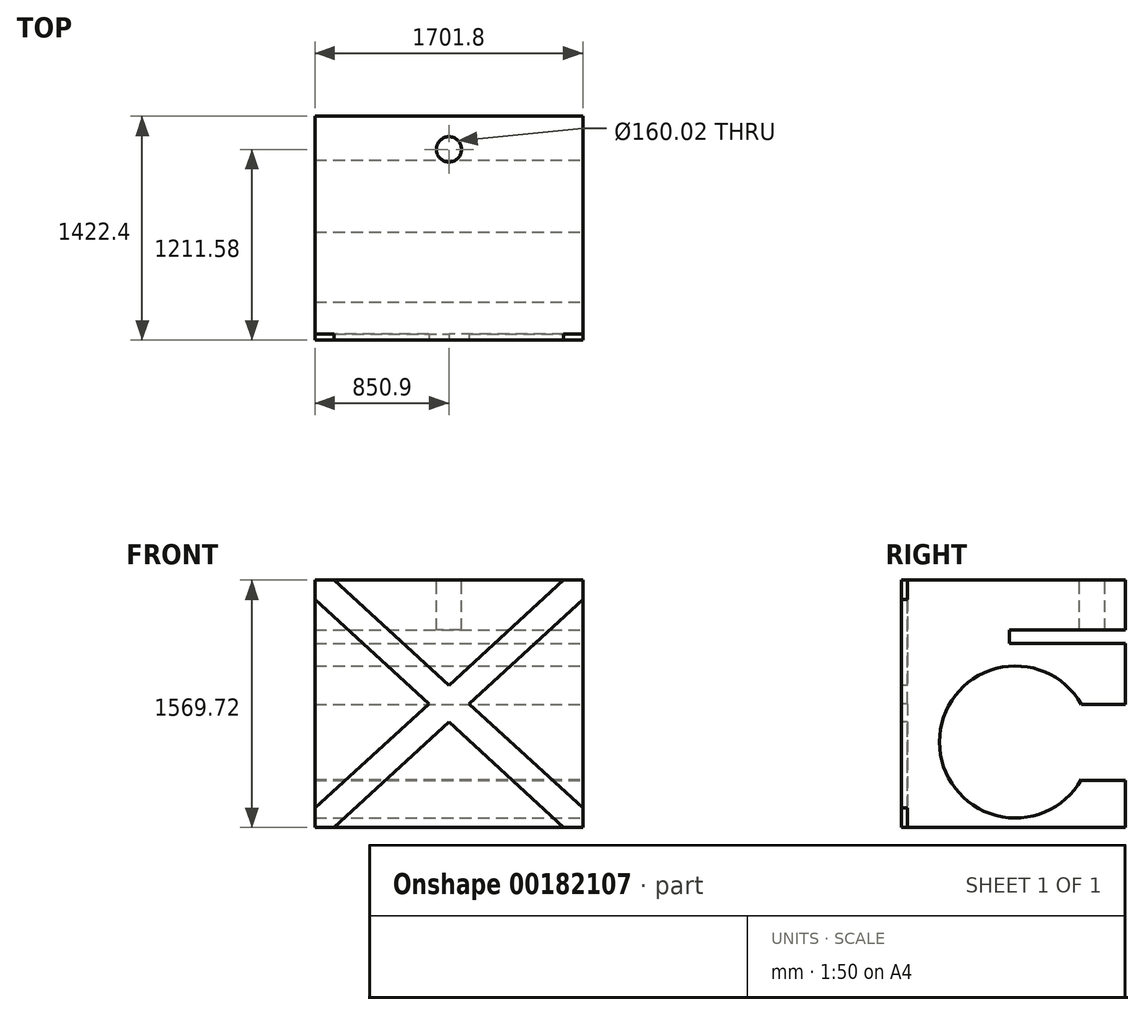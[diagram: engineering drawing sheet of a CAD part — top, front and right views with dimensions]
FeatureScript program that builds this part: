
annotation { "Feature Type Name" : "Feature", "Feature Type Description" : "" }
export const myFeature = defineFeature(function(context is Context, id is Id, definition is map)
    precondition{}
    {
        {
            var Q0;
            Q0=qCreatedBy(makeId("Front.planeOp"),FACE);
            var sketch = newSketch(context, id + "F0", { "sketchPlane" : qUnion([Q0])});
            skLineSegment(sketch, "E0.bottom", {"start": v(850.9, -784.86) * mm, "end": v(-850.9, -784.86) * mm});
            skLineSegment(sketch, "E0.top", {"start": v(850.9, 784.86) * mm, "end": v(-850.9, 784.86) * mm});
            skLineSegment(sketch, "E0.left", {"start": v(850.9, -784.86) * mm, "end": v(850.9, 784.86) * mm});
            skLineSegment(sketch, "E0.right", {"start": v(-850.9, -784.86) * mm, "end": v(-850.9, 784.86) * mm});
            skPoint(sketch, "E0.middle", {"position": v(0, 0) * mm});
            skSolve(sketch);
        }
        {
            var Q0;
            Q0 = qSketchRegion(id + "F0", true);
            extrude(context, id + "F1", {"entities" : qUnion([Q0]), "oppositeDirection" : true, "depth" : 1422.4 * mm});
        }
        {
            var Q0;
            Q0=makeQuery(id+"F1.opExtrude","CAP_FACE",FACE,{"disambiguationData":[OSD([sQuery(id+"F0.wireOp",EDGE,"E0.bottom"),sQuery(id+"F0.wireOp",EDGE,"E0.top"),sQuery(id+"F0.wireOp",EDGE,"E0.left"),sQuery(id+"F0.wireOp",EDGE,"E0.right")])],"isStart":true});
            var sketch = newSketch(context, id + "F2", { "sketchPlane" : qUnion([Q0])});
            skLineSegment(sketch, "E1", {"start": v(850.9, -784.86) * mm, "end": v(850.9, -662.94) * mm});
            skLineSegment(sketch, "E2", {"start": v(-850.9, 784.86) * mm, "end": v(-850.9, 662.94) * mm});
            skLineSegment(sketch, "E3", {"start": v(-850.9, -784.86) * mm, "end": v(-728.98, -784.86) * mm});
            skLineSegment(sketch, "E4", {"start": v(-850.9, -784.86) * mm, "end": v(-850.9, -662.94) * mm});
            skLineSegment(sketch, "E5", {"start": v(850.9, 784.86) * mm, "end": v(850.9, 662.94) * mm});
            skLineSegment(sketch, "E6", {"start": v(850.9, 784.86) * mm, "end": v(728.98, 784.86) * mm});
            skLineSegment(sketch, "E7", {"start": v(728.98, 784.86) * mm, "end": v(-850.9, -662.94) * mm});
            skLineSegment(sketch, "E8", {"start": v(-728.98, -784.86) * mm, "end": v(850.9, 662.94) * mm});
            skLineSegment(sketch, "E9", {"start": v(-850.9, 784.86) * mm, "end": v(-728.98, 784.86) * mm});
            skLineSegment(sketch, "E10", {"start": v(-728.98, 784.86) * mm, "end": v(850.9, -662.94) * mm});
            skLineSegment(sketch, "E11", {"start": v(850.9, -784.86) * mm, "end": v(728.98, -784.86) * mm});
            skLineSegment(sketch, "E12", {"start": v(728.98, -784.86) * mm, "end": v(-850.9, 662.94) * mm});
            skSolve(sketch);
        }
        {
            var Q0;
            {var subQ1=sQuery(id+"F2.wireOp",EDGE,"E1");Q0=makeQuery(id+"F2.imprint","IMPRINT",FACE,{"disambiguationData":[TD([[makeQuery(id+"F2.imprint","IMPRINT",EDGE,{"derivedFrom":subQ1}),1.0]])]});}
            var Q1;
            {var subQ1=sQuery(id+"F2.wireOp",EDGE,"E4");Q1=makeQuery(id+"F2.imprint","IMPRINT",FACE,{"disambiguationData":[TD([[makeQuery(id+"F2.imprint","IMPRINT",EDGE,{"derivedFrom":subQ1}),-1.0]])]});}
            var Q2;
            {var subQ0=sQuery(id+"F2.wireOp",EDGE,"E10");var subQ1=sQuery(id+"F2.wireOp",EDGE,"E7");var subQ2=makeQuery(id+"F2.imprint","INTERSECT",VERTEX,{"derivedFrom":[subQ1,subQ0]});Q2=makeQuery(id+"F2.imprint","IMPRINT",FACE,{"disambiguationData":[TD([[makeQuery(id+"F2.imprint","IMPRINT",EDGE,{"disambiguationData":[TD([[subQ2,-1.0]])],"derivedFrom":subQ1}),1.0]])]});}
            var Q3;
            {var subQ6=sQuery(id+"F2.wireOp",EDGE,"E2");Q3=makeQuery(id+"F2.imprint","IMPRINT",FACE,{"disambiguationData":[TD([[makeQuery(id+"F2.imprint","IMPRINT",EDGE,{"derivedFrom":subQ6}),-1.0]])]});}
            var Q4;
            {var subQ5=sQuery(id+"F2.wireOp",EDGE,"E5");Q4=makeQuery(id+"F2.imprint","IMPRINT",FACE,{"disambiguationData":[TD([[makeQuery(id+"F2.imprint","IMPRINT",EDGE,{"derivedFrom":subQ5}),1.0]])]});}
            extrude(context, id + "F3", {"entities" : qUnion([Q0, Q1, Q2, Q3, Q4]), "operationType" : NewBodyOperationType.REMOVE, "oppositeDirection" : true, "depth" : 38.1 * mm});
        }
        {
            var Q0;
            Q0=makeQuery(id+"F1.opExtrude","SWEPT_FACE",FACE,{"disambiguationData":[OSD([sQuery(id+"F0.wireOp",EDGE,"E0.top")])]});
            var sketch = newSketch(context, id + "F4", { "sketchPlane" : qUnion([Q0])});
            skLineSegment(sketch, "E13", {"start": v(-850.9, 1422.4) * mm, "end": v(0, 1422.4) * mm});
            skLineSegment(sketch, "E14", {"start": v(0, 1422.4) * mm, "end": v(0, 1211.58) * mm});
            skCircle(sketch, "E15", {"center": v(0, 1211.58) * mm, "radius": 80.01 * mm});
            skSolve(sketch);
        }
        {
            var Q0;
            Q0 = qSketchRegion(id + "F4", true);
            extrude(context, id + "F5", {"entities" : qUnion([Q0]), "operationType" : NewBodyOperationType.REMOVE, "oppositeDirection" : true, "depth" : 317.5 * mm});
        }
        {
            var Q0;
            Q0=makeQuery(id+"F1.opExtrude","SWEPT_FACE",FACE,{"disambiguationData":[OSD([sQuery(id+"F0.wireOp",EDGE,"E0.left")])]});
            var sketch = newSketch(context, id + "F6", { "sketchPlane" : qUnion([Q0])});
            skLineSegment(sketch, "E16", {"start": v(1422.4, 784.86) * mm, "end": v(1422.4, 467.36) * mm});
            skLineSegment(sketch, "E17", {"start": v(1422.4, 467.36) * mm, "end": v(1422.4, 383.54) * mm});
            skLineSegment(sketch, "E18", {"start": v(1422.4, 383.54) * mm, "end": v(685.8, 383.54) * mm});
            skLineSegment(sketch, "E19", {"start": v(685.8, 383.54) * mm, "end": v(685.8, 467.36) * mm});
            skLineSegment(sketch, "E20", {"start": v(1422.4, 467.36) * mm, "end": v(685.8, 467.36) * mm});
            skLineSegment(sketch, "E21", {"start": v(0, -784.86) * mm, "end": v(0, -99.06) * mm});
            skCircle(sketch, "E22", {"center": v(724.72, -242.8) * mm, "radius": 482.6 * mm});
            skLineSegment(sketch, "E23.bottom", {"start": v(1144.08, -3.97) * mm, "end": v(1422.4, -3.97) * mm});
            skLineSegment(sketch, "E23.top", {"start": v(1144.08, -486.57) * mm, "end": v(1422.4, -486.57) * mm});
            skLineSegment(sketch, "E23.left", {"start": v(1144.08, -3.97) * mm, "end": v(1144.08, -486.57) * mm});
            skLineSegment(sketch, "E23.right", {"start": v(1422.4, -3.97) * mm, "end": v(1422.4, -486.57) * mm});
            skSolve(sketch);
        }
        {
            var Q0;
            {var subQ0=sQuery(id+"F6.wireOp",EDGE,"E23.left");var subQ1=sQuery(id+"F6.wireOp",EDGE,"E22");var subQ3=makeQuery(id+"F6.imprint","INTERSECT",VERTEX,{"derivedFrom":[subQ1,subQ0]});Q0=makeQuery(id+"F6.imprint","IMPRINT",FACE,{"disambiguationData":[TD([[makeQuery(id+"F6.imprint","IMPRINT",EDGE,{"disambiguationData":[TD([[subQ3,1.0]])],"derivedFrom":subQ1}),1.0]])]});}
            var Q1;
            {var subQ0=sQuery(id+"F6.wireOp",EDGE,"E23.left");var subQ1=sQuery(id+"F6.wireOp",EDGE,"E22");var subQ3=makeQuery(id+"F6.imprint","INTERSECT",VERTEX,{"derivedFrom":[subQ1,subQ0]});Q1=makeQuery(id+"F6.imprint","IMPRINT",FACE,{"disambiguationData":[TD([[makeQuery(id+"F6.imprint","IMPRINT",EDGE,{"disambiguationData":[TD([[subQ3,-1.0]])],"derivedFrom":subQ1}),1.0]])]});}
            var Q2;
            {var subQ4=sQuery(id+"F6.wireOp",EDGE,"E23.bottom");Q2=makeQuery(id+"F6.imprint","IMPRINT",FACE,{"disambiguationData":[TD([[makeQuery(id+"F6.imprint","IMPRINT",EDGE,{"derivedFrom":subQ4}),-1.0]])]});}
            extrude(context, id + "F7", {"entities" : qUnion([Q0, Q1, Q2]), "operationType" : NewBodyOperationType.REMOVE, "oppositeDirection" : true, "depth" : 2110.74 * mm});
        }
        {
            var Q0;
            Q0=makeQuery(id+"F6.imprint","IMPRINT",FACE,{"disambiguationData":[TD([[makeQuery(id+"F6.imprint","IMPRINT",EDGE,{"derivedFrom":sQuery(id+"F6.wireOp",EDGE,"E17")}),1.0]])]});
            extrude(context, id + "F8", {"entities" : qUnion([Q0]), "operationType" : NewBodyOperationType.REMOVE, "oppositeDirection" : true, "depth" : 3215.64 * mm});
        }
    });
